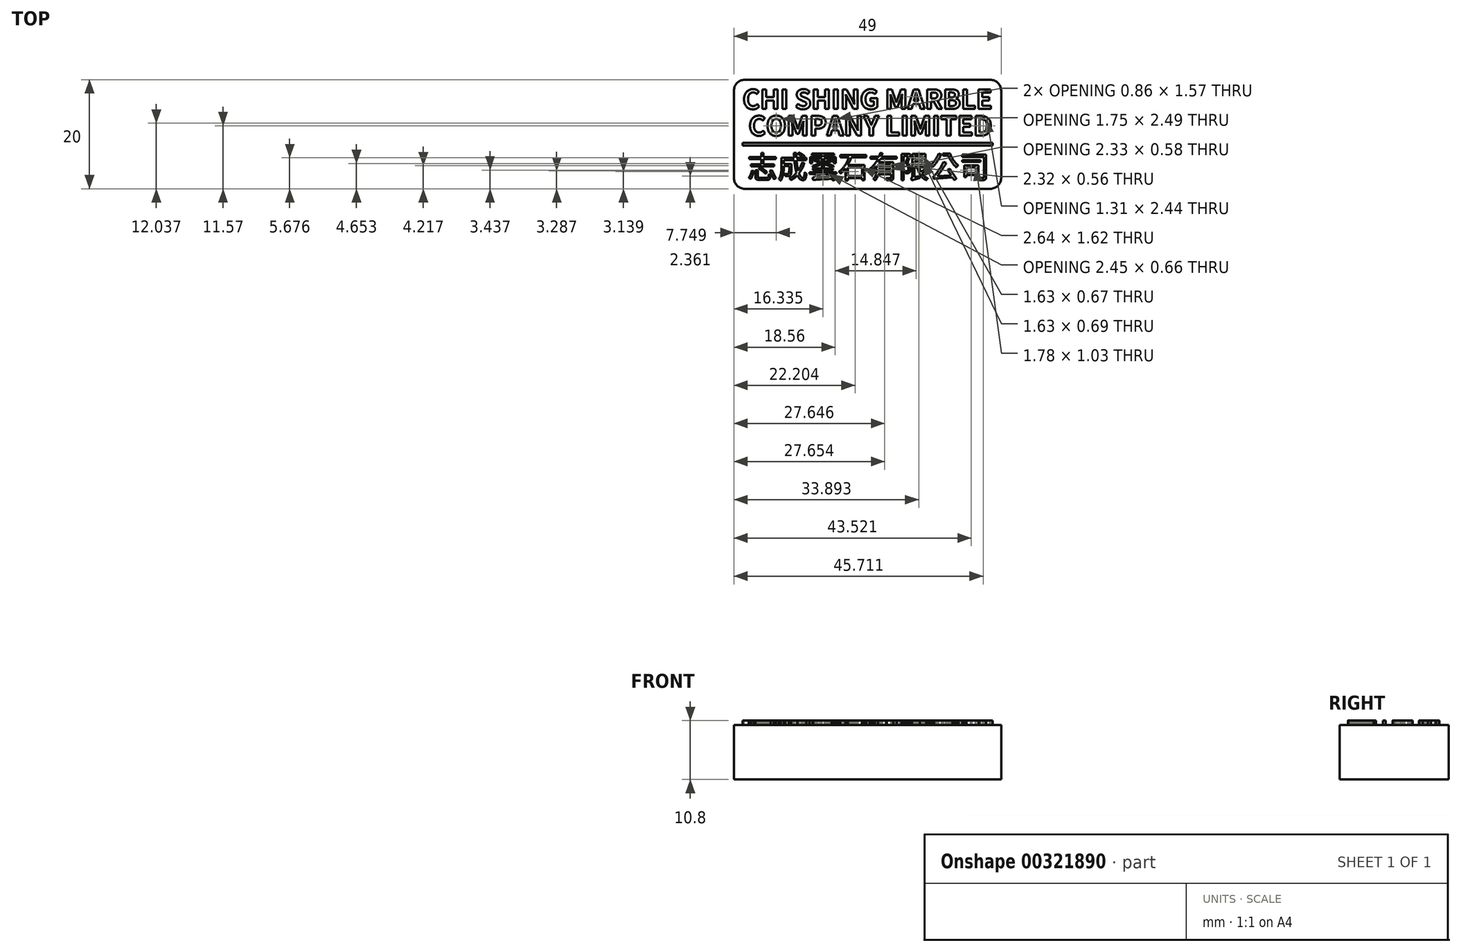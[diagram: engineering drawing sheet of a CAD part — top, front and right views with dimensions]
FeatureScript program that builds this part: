
annotation { "Feature Type Name" : "Feature", "Feature Type Description" : "" }
export const myFeature = defineFeature(function(context is Context, id is Id, definition is map)
    precondition{}
    {
        {
            var Q0;
            Q0=qCreatedBy(makeId("Top.planeOp"),FACE);
            var sketch = newSketch(context, id + "F0", { "sketchPlane" : qUnion([Q0])});
            skPoint(sketch, "E0.middle", {"position": v(0, 0) * mm});
            skText(sketch, "E1", { "text": "CHI SHING MARBLE \n COMPANY LIMITED ", "fontName": "NotoSansCJKtc-Bold.otf"});
            skText(sketch, "E2", { "text": "志成雲石有限公司", "fontName": "NotoSansCJKtc-Regular.otf"});
            skLineSegment(sketch, "E3.bottom", {"start": v(22.92, 0.25) * mm, "end": v(-22.92, 0.25) * mm});
            skLineSegment(sketch, "E3.top", {"start": v(22.92, -0.25) * mm, "end": v(-22.92, -0.25) * mm});
            skLineSegment(sketch, "E3.left", {"start": v(22.92, 0.25) * mm, "end": v(22.92, -0.25) * mm});
            skLineSegment(sketch, "E3.right", {"start": v(-22.92, 0.25) * mm, "end": v(-22.92, -0.25) * mm});
            skPoint(sketch, "E4.visualSharp", {"position": v(-25, 12) * mm});
            skPoint(sketch, "E5.visualSharp", {"position": v(25, 12) * mm});
            skPoint(sketch, "E6.visualSharp", {"position": v(25, -8) * mm});
            skPoint(sketch, "E7.visualSharp", {"position": v(-25, -8) * mm});
            const initialGuessF0  = {"E1": [-0.02292, 0.00643, 1, 0, 0.0035], "E2": [-0.02206, -0.00623, 1, 0, 0.004]};
            skSetInitialGuess(sketch, initialGuessF0);
            skSolve(sketch);
        }
        {
            var Q0;
            Q0=qCreatedBy(makeId("Top.planeOp"),FACE);
            var sketch = newSketch(context, id + "F1", { "sketchPlane" : qUnion([Q0])});
            skLineSegment(sketch, "E8.bottom", {"start": v(22.5, -8.2) * mm, "end": v(-22.5, -8.2) * mm});
            skLineSegment(sketch, "E8.top", {"start": v(22.5, 11.8) * mm, "end": v(-22.5, 11.8) * mm});
            skLineSegment(sketch, "E8.left", {"start": v(24.5, -6.2) * mm, "end": v(24.5, 9.8) * mm});
            skLineSegment(sketch, "E8.right", {"start": v(-24.5, -6.2) * mm, "end": v(-24.5, 9.8) * mm});
            skPoint(sketch, "E8.middle", {"position": v(0, 1.8) * mm});
            skPoint(sketch, "E8.middle.positionSnap0", {"position": v(0, 3.1) * mm});
            skPoint(sketch, "E8.centerSnap0", {"position": v(0, 3.1) * mm});
            skPoint(sketch, "E9.visualSharp", {"position": v(-24.5, 11.8) * mm});
            skArc(sketch, "E9.filletArc", {"start": v(-22.5, 11.8) * mm, "mid": v(-23.91, 11.21) * mm, "end": v(-24.5, 9.8) * mm});
            skPoint(sketch, "E10.visualSharp", {"position": v(24.5, 11.8) * mm});
            skArc(sketch, "E10.filletArc", {"start": v(24.5, 9.8) * mm, "mid": v(23.91, 11.21) * mm, "end": v(22.5, 11.8) * mm});
            skPoint(sketch, "E11.visualSharp", {"position": v(24.5, -8.2) * mm});
            skArc(sketch, "E11.filletArc", {"start": v(22.5, -8.2) * mm, "mid": v(23.91, -7.61) * mm, "end": v(24.5, -6.2) * mm});
            skPoint(sketch, "E12.visualSharp", {"position": v(-24.5, -8.2) * mm});
            skArc(sketch, "E12.filletArc", {"start": v(-24.5, -6.2) * mm, "mid": v(-23.91, -7.61) * mm, "end": v(-22.5, -8.2) * mm});
            skSolve(sketch);
        }
        {
            var Q0;
            Q0=makeQuery(id+"F1.imprint","IMPRINT",FACE,{"disambiguationData":[TD([[makeQuery(id+"F1.imprint","IMPRINT",EDGE,{"derivedFrom":sQuery(id+"F1.wireOp",EDGE,"E8.bottom")}),-1.0]])]});
            var Q1;
            Q1=makeQuery(id+"F1.imprint","IMPRINT",FACE,{"disambiguationData":[TD([[makeQuery(id+"F1.imprint","IMPRINT",EDGE,{"derivedFrom":makeQuery(id+"F3.opExtrude","CAP_EDGE",EDGE,{"disambiguationData":[OSD([sQuery(id+"F0.wireOp",EDGE,"E3.bottom")])],"isStart":true})}),-1.0]])]});
            extrude(context, id + "F2", {"entities" : qUnion([Q0, Q1]), "oppositeDirection" : true, "depth" : 10 * mm});
        }
        {
            var Q0;
            Q0 = qSketchRegion(id + "F0", true);
            extrude(context, id + "F3", {"entities" : qUnion([Q0]), "depth" : 0.8 * mm});
        }
        {
            var Q0;
            Q0=makeQuery(id+"F3.opExtrude","SWEPT_BODY",BODY,{"disambiguationData":[OSD([sQuery(id+"F0.wireOp",EDGE,"E2.sketch_text.stroke-38"),sQuery(id+"F0.wireOp",EDGE,"E2.sketch_text.stroke-39"),sQuery(id+"F0.wireOp",EDGE,"E2.sketch_text.stroke-40"),sQuery(id+"F0.wireOp",EDGE,"E2.sketch_text.stroke-41")])]});
            transform(context, id + "F4", {"entities" : qUnion([Q0]), "transformType" : TransformType.TRANSLATION_3D, "dx" : -0.02 * mm, "dy" : 0.07 * mm, "dz" : 0 * mm, "makeCopy" : false});
        }
    });
